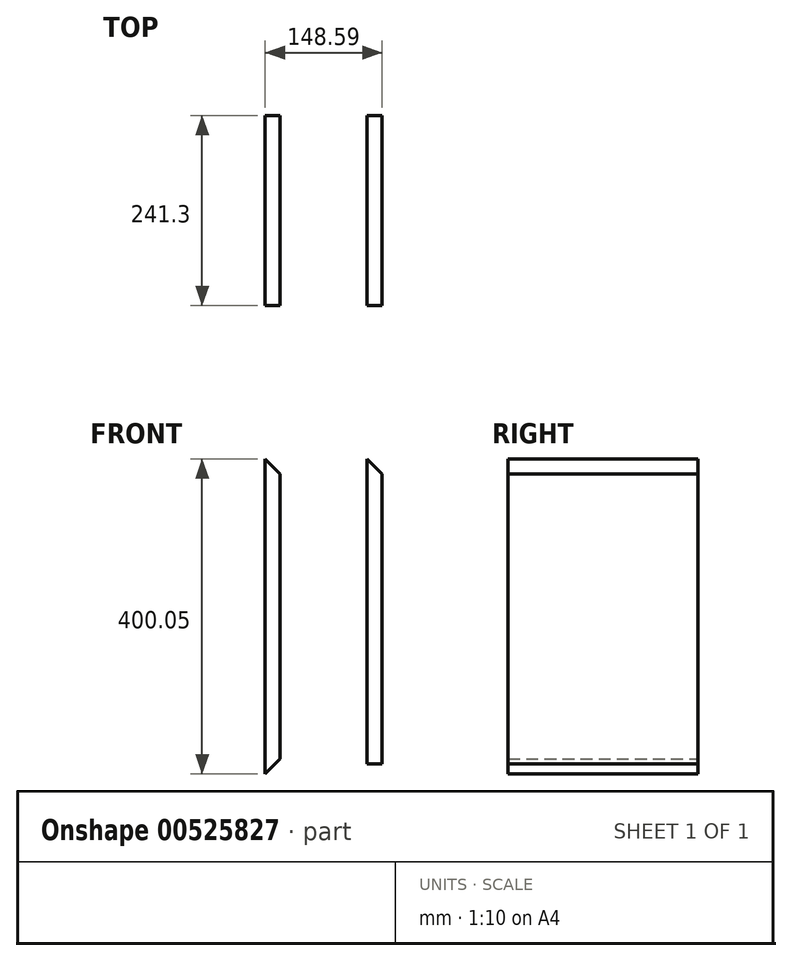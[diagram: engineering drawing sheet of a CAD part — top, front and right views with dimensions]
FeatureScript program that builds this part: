
annotation { "Feature Type Name" : "Feature", "Feature Type Description" : "" }
export const myFeature = defineFeature(function(context is Context, id is Id, definition is map)
    precondition{}
    {
        {
            var Q0;
            Q0=qCreatedBy(makeId("Front.planeOp"),FACE);
            var sketch = newSketch(context, id + "F0", { "sketchPlane" : qUnion([Q0])});
            skLineSegment(sketch, "E0.left", {"start": v(-9.53, 342.98) * mm, "end": v(-9.53, -57.07) * mm});
            skLineSegment(sketch, "E0.right", {"start": v(9.52, 323.93) * mm, "end": v(9.52, -38.02) * mm});
            skPoint(sketch, "E0.middle", {"position": v(0, 0) * mm});
            skLineSegment(sketch, "E1", {"start": v(-9.53, 342.98) * mm, "end": v(9.52, 323.93) * mm});
            skLineSegment(sketch, "E2", {"start": v(-9.53, -57.07) * mm, "end": v(9.52, -38.02) * mm});
            skSolve(sketch);
        }
        {
            var Q0;
            Q0=qSketchRegion(id+"F0",true);
            extrude(context, id + "F1", {"entities" : qUnion([Q0]), "depth" : 241.3 * mm});
        }
        {
            var Q0;
            Q0=makeQuery(id+"F1.opExtrude","SWEPT_BODY",BODY,{"disambiguationData":[OSD([sQuery(id+"F0.wireOp",EDGE,"E0.left"),sQuery(id+"F0.wireOp",EDGE,"E0.right"),sQuery(id+"F0.wireOp",EDGE,"E1"),sQuery(id+"F0.wireOp",EDGE,"E2")])]});
            transform(context, id + "F2", {"entities" : qUnion([Q0]), "transformType" : TransformType.TRANSLATION_3D, "dx" : 129.54 * mm, "dy" : 0 * mm, "dz" : 0 * mm, "makeCopy" : true});
        }
        {
            var Q0;
            Q0=makeQuery(id+"F2.opPattern","COPY",FACE,{"derivedFrom":makeQuery(id+"F1.opExtrude","CAP_FACE",FACE,{"disambiguationData":[OSD([sQuery(id+"F0.wireOp",EDGE,"E0.left"),sQuery(id+"F0.wireOp",EDGE,"E0.right"),sQuery(id+"F0.wireOp",EDGE,"E1"),sQuery(id+"F0.wireOp",EDGE,"E2")])],"isStart":false}),"instanceName":"1"});
            var sketch = newSketch(context, id + "F3", { "sketchPlane" : qUnion([Q0])});
            skLineSegment(sketch, "E3", {"start": v(120.02, -57.07) * mm, "end": v(139.06, -38.02) * mm});
            skLineSegment(sketch, "E4", {"start": v(139.06, -38.02) * mm, "end": v(139.06, -57.07) * mm});
            skLineSegment(sketch, "E5", {"start": v(139.06, -57.07) * mm, "end": v(120.02, -57.07) * mm});
            skSolve(sketch);
        }
        {
            var Q0;
            Q0=qSketchRegion(id+"F3",true);
            extrude(context, id + "F4", {"entities" : qUnion([Q0]), "operationType" : NewBodyOperationType.ADD, "oppositeDirection" : true, "depth" : 241.3 * mm});
        }
        {
            var Q0;
            Q0=makeQuery(id+"F4.boolean.opBoolean","MERGE",FACE,{"derivedFrom":[makeQuery(id+"F2.opPattern","COPY",FACE,{"derivedFrom":makeQuery(id+"F1.opExtrude","CAP_FACE",FACE,{"disambiguationData":[OSD([sQuery(id+"F0.wireOp",EDGE,"E0.left"),sQuery(id+"F0.wireOp",EDGE,"E0.right"),sQuery(id+"F0.wireOp",EDGE,"E1"),sQuery(id+"F0.wireOp",EDGE,"E2")])],"isStart":false}),"instanceName":"1"}),makeQuery(id+"F4.opExtrude","CAP_FACE",FACE,{"disambiguationData":[OSD([sQuery(id+"F3.wireOp",EDGE,"E3"),sQuery(id+"F3.wireOp",EDGE,"E4"),sQuery(id+"F3.wireOp",EDGE,"E5")])],"isStart":true})]});
            var sketch = newSketch(context, id + "F5", { "sketchPlane" : qUnion([Q0])});
            skLineSegment(sketch, "E6.bottom", {"start": v(120.02, -57.07) * mm, "end": v(139.06, -57.07) * mm});
            skLineSegment(sketch, "E6.top", {"start": v(120.02, -44.37) * mm, "end": v(139.06, -44.37) * mm});
            skLineSegment(sketch, "E6.left", {"start": v(120.02, -57.07) * mm, "end": v(120.02, -44.37) * mm});
            skLineSegment(sketch, "E6.right", {"start": v(139.06, -57.07) * mm, "end": v(139.06, -44.37) * mm});
            skSolve(sketch);
        }
        {
            var Q0;
            Q0=qSketchRegion(id+"F5",true);
            extrude(context, id + "F6", {"entities" : qUnion([Q0]), "operationType" : NewBodyOperationType.REMOVE, "endBound" : BoundingType.THROUGH_ALL, "oppositeDirection" : true, "depth" : 25.4 * mm});
        }
    });
